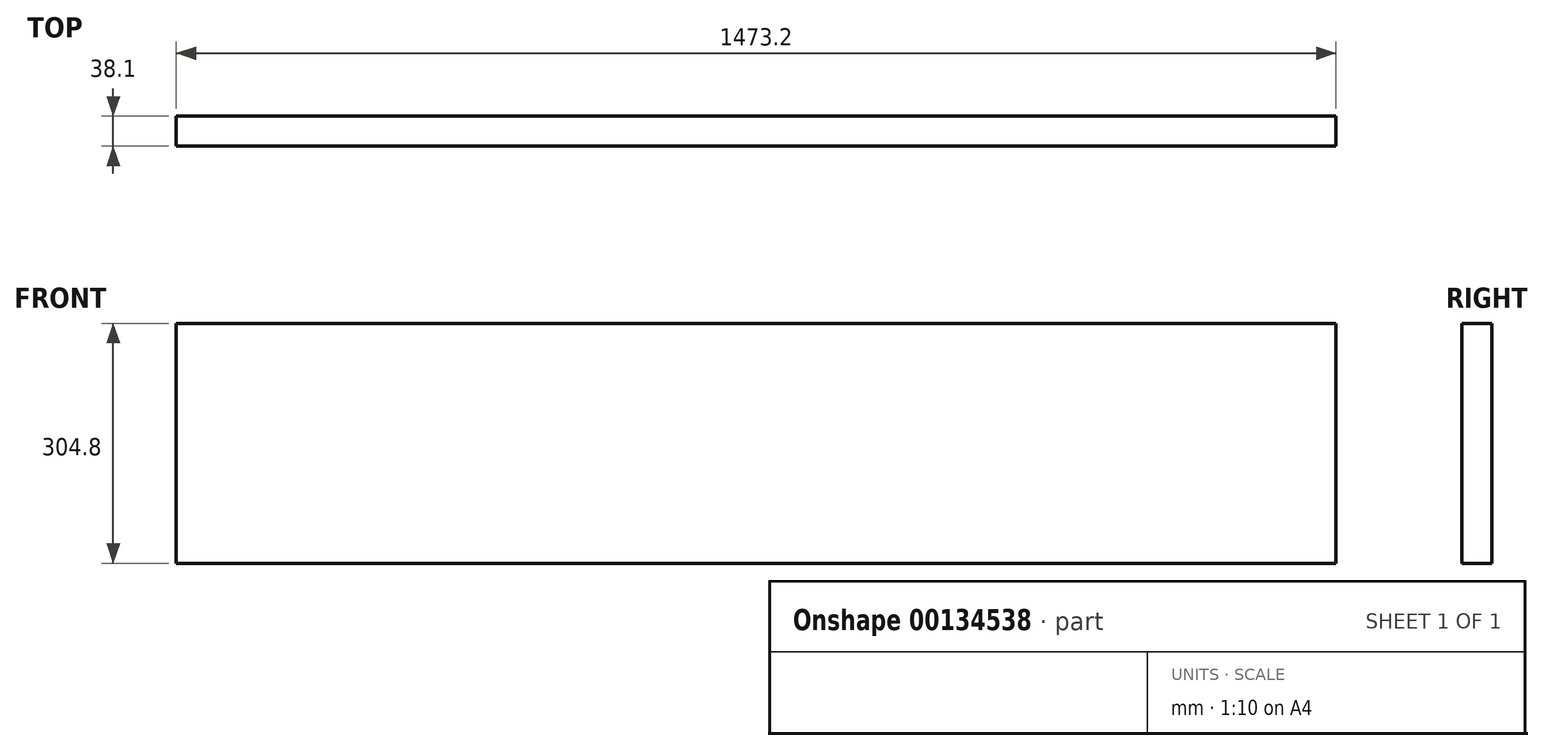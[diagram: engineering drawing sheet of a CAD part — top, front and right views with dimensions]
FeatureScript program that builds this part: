
annotation { "Feature Type Name" : "Feature", "Feature Type Description" : "" }
export const myFeature = defineFeature(function(context is Context, id is Id, definition is map)
    precondition{}
    {
        {
            var Q0;
            Q0=qCreatedBy(makeId("Front.planeOp"),FACE);
            var sketch = newSketch(context, id + "F0", { "sketchPlane" : qUnion([Q0])});
            skLineSegment(sketch, "E0", {"start": v(-73.28, -25.93) * mm, "end": v(1399.92, -25.93) * mm});
            skLineSegment(sketch, "E1", {"start": v(1399.92, -25.93) * mm, "end": v(1399.92, 278.87) * mm});
            skLineSegment(sketch, "E2", {"start": v(1399.92, 278.87) * mm, "end": v(-73.28, 278.87) * mm});
            skLineSegment(sketch, "E3", {"start": v(-73.28, 278.87) * mm, "end": v(-73.28, -25.93) * mm});
            skSolve(sketch);
        }
        {
            var Q0;
            Q0=makeQuery(id+"F0.imprint","IMPRINT",FACE,{"disambiguationData":[TD([[makeQuery(id+"F0.imprint","IMPRINT",EDGE,{"derivedFrom":sQuery(id+"F0.wireOp",EDGE,"E0")}),1.0]])]});
            extrude(context, id + "F1", {"entities" : qUnion([Q0]), "depth" : 38.1 * mm});
        }
    });
